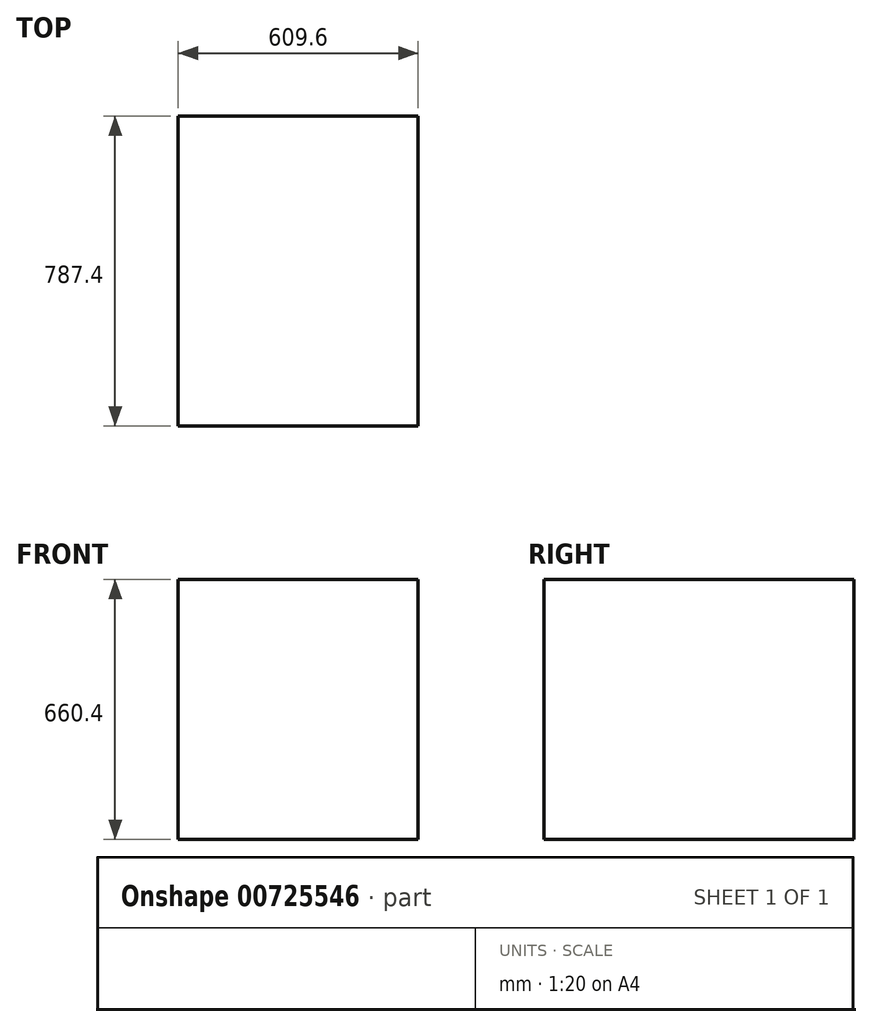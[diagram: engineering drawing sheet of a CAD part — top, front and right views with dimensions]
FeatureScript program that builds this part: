
annotation { "Feature Type Name" : "Feature", "Feature Type Description" : "" }
export const myFeature = defineFeature(function(context is Context, id is Id, definition is map)
    precondition{}
    {
        {
            var Q0;
            Q0=qCreatedBy(makeId("Top.planeOp"),FACE);
            var sketch = newSketch(context, id + "F0", { "sketchPlane" : qUnion([Q0])});
            skLineSegment(sketch, "E0.bottom", {"start": v(304.8, 393.7) * mm, "end": v(-304.8, 393.7) * mm});
            skLineSegment(sketch, "E0.top", {"start": v(304.8, -393.7) * mm, "end": v(-304.8, -393.7) * mm});
            skLineSegment(sketch, "E0.left", {"start": v(304.8, 393.7) * mm, "end": v(304.8, -393.7) * mm});
            skLineSegment(sketch, "E0.right", {"start": v(-304.8, 393.7) * mm, "end": v(-304.8, -393.7) * mm});
            skPoint(sketch, "E0.middle", {"position": v(0, 0) * mm});
            skSolve(sketch);
        }
        {
            var Q0;
            Q0 = qSketchRegion(id + "F0", true);
            extrude(context, id + "F1", {"entities" : qUnion([Q0]), "depth" : 660.4 * mm, "offsetDistance" : 25.4 * mm});
        }
    });
